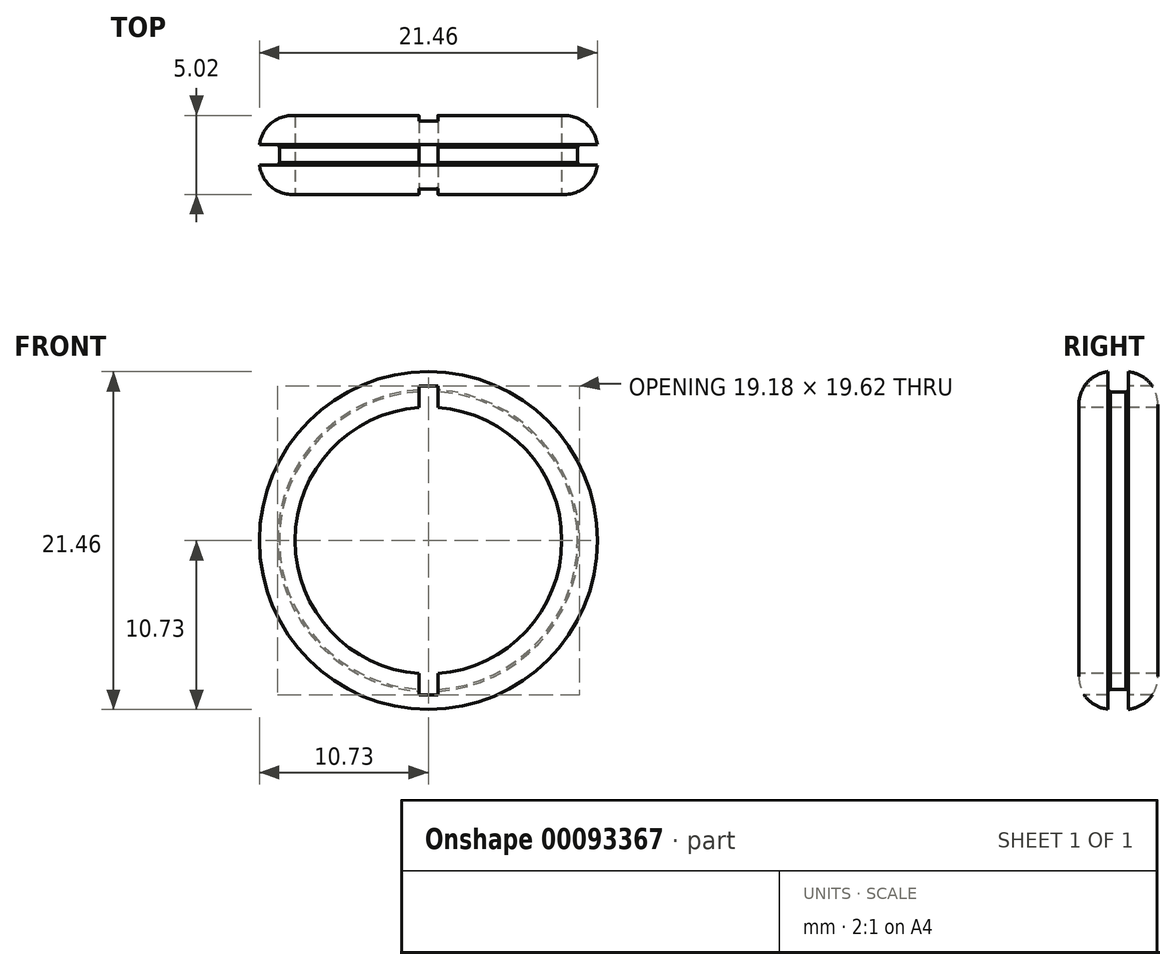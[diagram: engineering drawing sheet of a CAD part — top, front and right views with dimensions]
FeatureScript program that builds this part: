
annotation { "Feature Type Name" : "Feature", "Feature Type Description" : "" }
export const myFeature = defineFeature(function(context is Context, id is Id, definition is map)
    precondition{}
    {
        {
            var Q0;
            Q0=qCreatedBy(makeId("Front.planeOp"),FACE);
            var sketch = newSketch(context, id + "F0", { "sketchPlane" : qUnion([Q0])});
            skCircle(sketch, "E0", {"center": v(0, 0) * mm, "radius": 8.88 * mm});
            skPoint(sketch, "E1", {"position": v(0, 8.88) * mm});
            skSolve(sketch);
        }
        {
            var Q0;
            Q0=qCreatedBy(makeId("Right.planeOp"),FACE);
            var sketch = newSketch(context, id + "F1", { "sketchPlane" : qUnion([Q0])});
            skLineSegment(sketch, "E2", {"start": v(0, 8.47) * mm, "end": v(-2.5, 8.47) * mm});
            skLineSegment(sketch, "E3", {"start": v(-2.5, 8.47) * mm, "end": v(-2.8, 10.25) * mm});
            skLineSegment(sketch, "E4", {"start": v(-2.8, 10.25) * mm, "end": v(-0.65, 10.73) * mm});
            skLineSegment(sketch, "E5", {"start": v(-0.65, 10.73) * mm, "end": v(-0.65, 9.59) * mm});
            skLineSegment(sketch, "E6", {"start": v(-0.65, 9.59) * mm, "end": v(-0.5, 9.47) * mm});
            skLineSegment(sketch, "E7", {"start": v(-0.5, 9.47) * mm, "end": v(0, 9.47) * mm});
            skLineSegment(sketch, "E8.MirrorCS", {"start": v(0.65, 9.59) * mm, "end": v(0.5, 9.47) * mm});
            skLineSegment(sketch, "E9.MirrorCS", {"start": v(2.8, 10.25) * mm, "end": v(0.65, 10.73) * mm});
            skLineSegment(sketch, "E10.MirrorCS", {"start": v(0.65, 10.73) * mm, "end": v(0.65, 9.59) * mm});
            skLineSegment(sketch, "E11.MirrorCS", {"start": v(2.5, 8.47) * mm, "end": v(2.8, 10.25) * mm});
            skLineSegment(sketch, "E12.MirrorCS", {"start": v(0, 8.47) * mm, "end": v(2.5, 8.47) * mm});
            skLineSegment(sketch, "E13.MirrorCS", {"start": v(0.5, 9.47) * mm, "end": v(0, 9.47) * mm});
            skSolve(sketch);
        }
        {
            var Q0;
            Q0=makeQuery(id+"F1.imprint","IMPRINT",FACE,{"disambiguationData":[TD([[makeQuery(id+"F1.imprint","IMPRINT",EDGE,{"derivedFrom":sQuery(id+"F1.wireOp",EDGE,"E2")}),-1.0]])]});
            var Q1;
            Q1=sQuery(id+"F0.wireOp",EDGE,"E0");
            sweep(context, id + "F2", {"profiles" : qUnion([Q0]), "path" : qUnion([Q1])});
        }
        {
            var Q0;
            Q0=makeQuery(id+"F2.opSweep","SWEPT_EDGE",EDGE,{"disambiguationData":[OSD([sQuery(id+"F0.wireOp",EDGE,"E0"),sQuery(id+"F1.wireOp",EDGE,"E3"),sQuery(id+"F1.wireOp",EDGE,"E4")])]});
            var Q1;
            Q1=makeQuery(id+"F2.opSweep","SWEPT_EDGE",EDGE,{"disambiguationData":[OSD([sQuery(id+"F0.wireOp",EDGE,"E0"),sQuery(id+"F1.wireOp",EDGE,"E9.MirrorCS"),sQuery(id+"F1.wireOp",EDGE,"E11.MirrorCS")])]});
            fillet(context, id + "F3", {"entities" : qUnion([Q0, Q1]), "radius" : 2.07 * mm, "tangentPropagation" : true, "allowEdgeOverflow" : false});
        }
        {
            var Q0;
            Q0=qCreatedBy(makeId("Front.planeOp"),FACE);
            var sketch = newSketch(context, id + "F4", { "sketchPlane" : qUnion([Q0])});
            skLineSegment(sketch, "E14.bottom", {"start": v(-0.6, 9.81) * mm, "end": v(0.6, 9.81) * mm});
            skLineSegment(sketch, "E14.top", {"start": v(-0.6, -9.81) * mm, "end": v(0.6, -9.81) * mm});
            skLineSegment(sketch, "E14.left", {"start": v(-0.6, 9.81) * mm, "end": v(-0.6, -9.81) * mm});
            skLineSegment(sketch, "E14.right", {"start": v(0.6, 9.81) * mm, "end": v(0.6, -9.81) * mm});
            skPoint(sketch, "E14.middle", {"position": v(0, 0) * mm});
            skSolve(sketch);
        }
        {
            var Q0;
            Q0=qSketchRegion(id+"F4",true);
            extrude(context, id + "F5", {"entities" : qUnion([Q0]), "operationType" : NewBodyOperationType.REMOVE, "oppositeDirection" : true, "depth" : 25 * mm, "hasSecondDirection" : true, "secondDirectionOppositeDirection" : false, "secondDirectionDepth" : 25 * mm});
        }
    });
